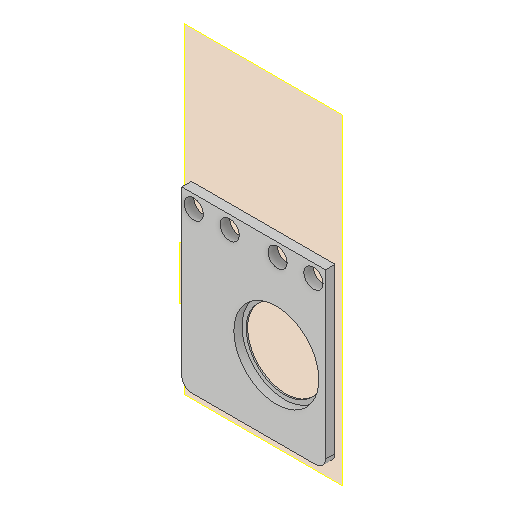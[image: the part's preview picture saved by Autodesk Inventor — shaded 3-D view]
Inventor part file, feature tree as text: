
AUTODESK INVENTOR PART (.ipt)
format: ipt  version: 2022 (Build 260153000, 153)  size: 132,608 bytes
history: native  units: mm
features: plane x2, extrude x2, sketch x2, other x2, reference x1
ambient origin geometry x8: Origin, YZ Plane, XZ Plane, XY Plane, X Axis, Y Axis, Z Axis, Center Point
bodies: Solid1 (feature_tree)
feature tree (9):
  plane  "Work Plane1"
  plane  "Work Plane2"
  extrude  "Extrusion2"  Depth=0.6mm TaperAngle=0.0deg
  extrude  "Extrusion3"  Depth=32.0mm
  sketch  "Sketch2"  dims[d3=4.0mm d4=0.0mm d8=0.6mm d9=0.0mm]
  reference  "Reference5"
  sketch  "Sketch3"  dims[d11=35.5mm d12=32.0mm]
  other  "Assembly_XY_stage_with_motors_v3.iam"
  other  "00_SMLM_chamber:1"
